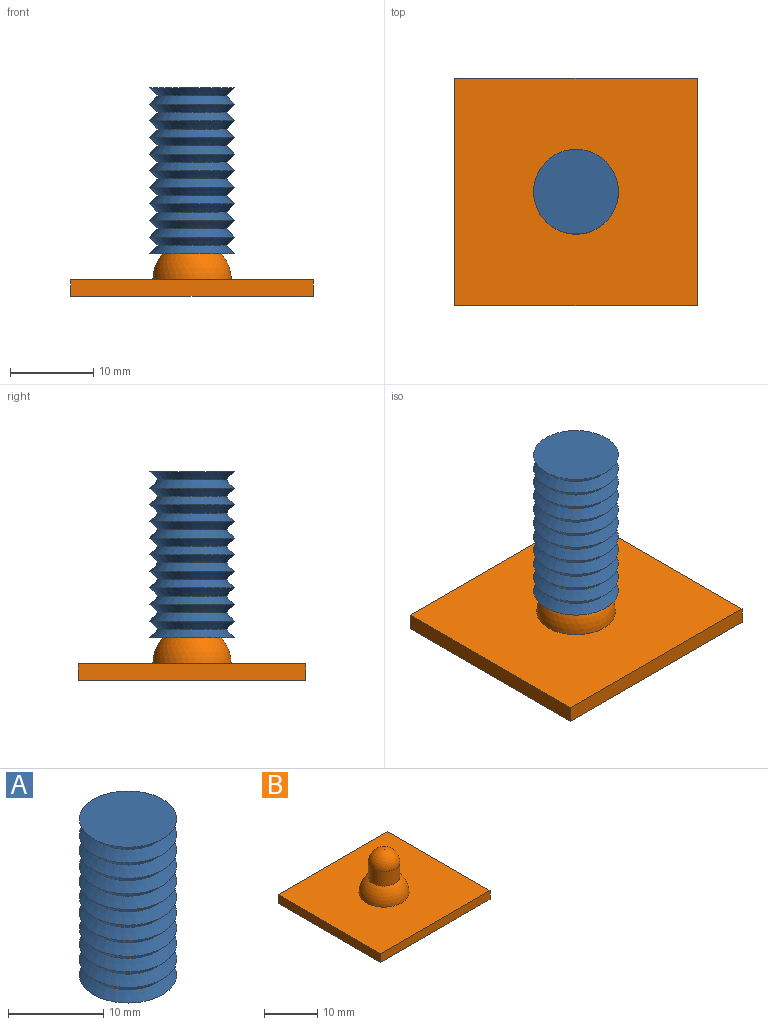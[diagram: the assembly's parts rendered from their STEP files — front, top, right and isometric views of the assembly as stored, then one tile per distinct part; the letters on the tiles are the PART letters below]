
ASSEMBLY  parts=2 mates=1
PART A: 25 faces, bbox 10.4x10.4x20 mm
  f0: cone r=4.1mm half-angle=45deg, axis (0,0,-1), area 40.9mm2, adj f1,f23
  f1: cone r=5.1mm half-angle=45deg, axis (0,0,1), area 40.9mm2, adj f0,f2
  f2: cone r=4.1mm half-angle=45deg, axis (0,0,-1), area 40.9mm2, adj f1,f3
  f3: cone r=5.1mm half-angle=45deg, axis (0,0,1), area 40.9mm2, adj f2,f4
  f4: cone r=4.1mm half-angle=45deg, axis (0,0,-1), area 40.9mm2, adj f3,f5
  f5: cone r=5.1mm half-angle=45deg, axis (0,0,1), area 40.9mm2, adj f4,f6
  f6: cone r=4.1mm half-angle=45deg, axis (0,0,-1), area 40.9mm2, adj f5,f7
  f7: cone r=5.1mm half-angle=45deg, axis (0,0,1), area 40.9mm2, adj f6,f8
  f8: cone r=4.1mm half-angle=45deg, axis (0,0,-1), area 40.9mm2, adj f7,f9
  f9: cone r=5.1mm half-angle=45deg, axis (0,0,1), area 40.9mm2, adj f8,f10
  f10: cone r=4.1mm half-angle=45deg, axis (0,0,-1), area 40.9mm2, adj f9,f11
  f11: cone r=5.1mm half-angle=45deg, axis (0,0,1), area 40.9mm2, adj f10,f12
  f12: cone r=4.1mm half-angle=45deg, axis (0,0,-1), area 40.9mm2, adj f11,f13
  f13: cone r=5.1mm half-angle=45deg, axis (0,0,1), area 40.9mm2, adj f12,f14
  f14: cone r=4.1mm half-angle=45deg, axis (0,0,-1), area 40.9mm2, adj f13,f15
  f15: plane 10.2x10.2mm, normal (0,0,-1), area 28.9mm2, adj f14,f24
  f16: cylinder r=3.1mm len=8mm, axis (0,0,1), area 155.8mm2, adj f17,f24
  f17: plane 6.2x6.2mm, normal (0,0,-1), area 30.2mm2, adj f16
  f18: plane 10.2x10.2mm, normal (0,0,1), area 81.7mm2, adj f19
  f19: cone r=5.1mm half-angle=45deg, axis (0,0,1), area 40.9mm2, adj f18,f20
  f20: cone r=4.1mm half-angle=45deg, axis (0,0,-1), area 40.9mm2, adj f19,f21
  f21: cone r=5.1mm half-angle=45deg, axis (0,0,1), area 40.9mm2, adj f20,f22
  f22: cone r=4.1mm half-angle=45deg, axis (0,0,-1), area 40.9mm2, adj f21,f23
  f23: cone r=5.1mm half-angle=45deg, axis (0,0,1), area 40.9mm2, adj f0,f22
  f24: torus R=4.1mm, axis (0,0,1), area 34.2mm2, adj f15,f16
PART B: 9 faces, bbox 29.2x27.3x12 mm
  f0: plane 29.19x27.35mm, normal (0,0,1), area 728.2mm2, adj f3,f4,f5,f6,f7
  f1: sphere r=3mm, area 56.5mm2, adj f2
  f2: cylinder r=3mm len=6mm, axis (0,0,1), area 63.2mm2, adj f1,f3
  f3: sphere r=4.72mm, area 108.3mm2, adj f0,f2
  f4: plane 29.19x2mm, normal (0,-1,0), area 58.4mm2, adj f0,f5,f7,f8
  f5: plane 27.35x2mm, normal (1,0,0), area 54.7mm2, adj f0,f4,f6,f8
  f6: plane 29.19x2mm, normal (0,1,0), area 58.4mm2, adj f0,f5,f7,f8
  f7: plane 27.35x2mm, normal (-1,0,0), area 54.7mm2, adj f0,f4,f6,f8
  f8: plane 29.19x27.35mm, normal (0,0,-1), area 798.3mm2, adj f4,f5,f6,f7
PLACE A t=(0,0,30.85)mm
PLACE B t=(0,0,27.7)mm
MATE revolute B.f2 <-> A.f0  axis (0,0,1) through (0,0,31.35)mm
